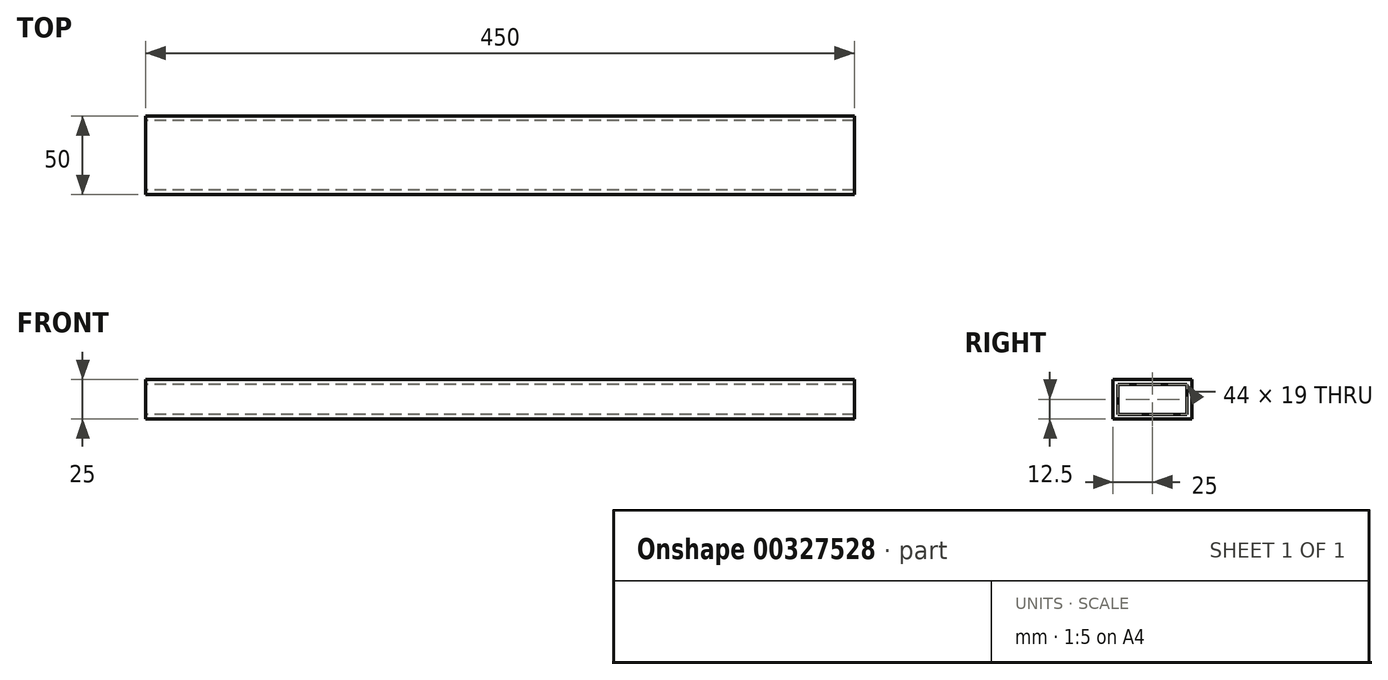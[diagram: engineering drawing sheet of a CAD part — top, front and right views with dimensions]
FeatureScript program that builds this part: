
annotation { "Feature Type Name" : "Feature", "Feature Type Description" : "" }
export const myFeature = defineFeature(function(context is Context, id is Id, definition is map)
    precondition{}
    {
        {
            var Q0;
            Q0=qCreatedBy(makeId("Right.planeOp"),FACE);
            var sketch = newSketch(context, id + "F0", { "sketchPlane" : qUnion([Q0])});
            skLineSegment(sketch, "E0.bottom", {"start": v(-25, 12.5) * mm, "end": v(25, 12.5) * mm});
            skLineSegment(sketch, "E0.top", {"start": v(-25, -12.5) * mm, "end": v(25, -12.5) * mm});
            skLineSegment(sketch, "E0.left", {"start": v(-25, 12.5) * mm, "end": v(-25, -12.5) * mm});
            skLineSegment(sketch, "E0.right", {"start": v(25, 12.5) * mm, "end": v(25, -12.5) * mm});
            skPoint(sketch, "E0.middle", {"position": v(0, 0) * mm});
            skLineSegment(sketch, "E1.bottom", {"start": v(-22, 9.5) * mm, "end": v(22, 9.5) * mm});
            skLineSegment(sketch, "E1.top", {"start": v(-22, -9.5) * mm, "end": v(22, -9.5) * mm});
            skLineSegment(sketch, "E1.left", {"start": v(-22, 9.5) * mm, "end": v(-22, -9.5) * mm});
            skLineSegment(sketch, "E1.right", {"start": v(22, 9.5) * mm, "end": v(22, -9.5) * mm});
            skSolve(sketch);
        }
        {
            var Q0;
            Q0 = qSketchRegion(id + "F0", true);
            extrude(context, id + "F1", {"entities" : qUnion([Q0]), "depth" : 450 * mm, "symmetric" : true});
        }
    });
